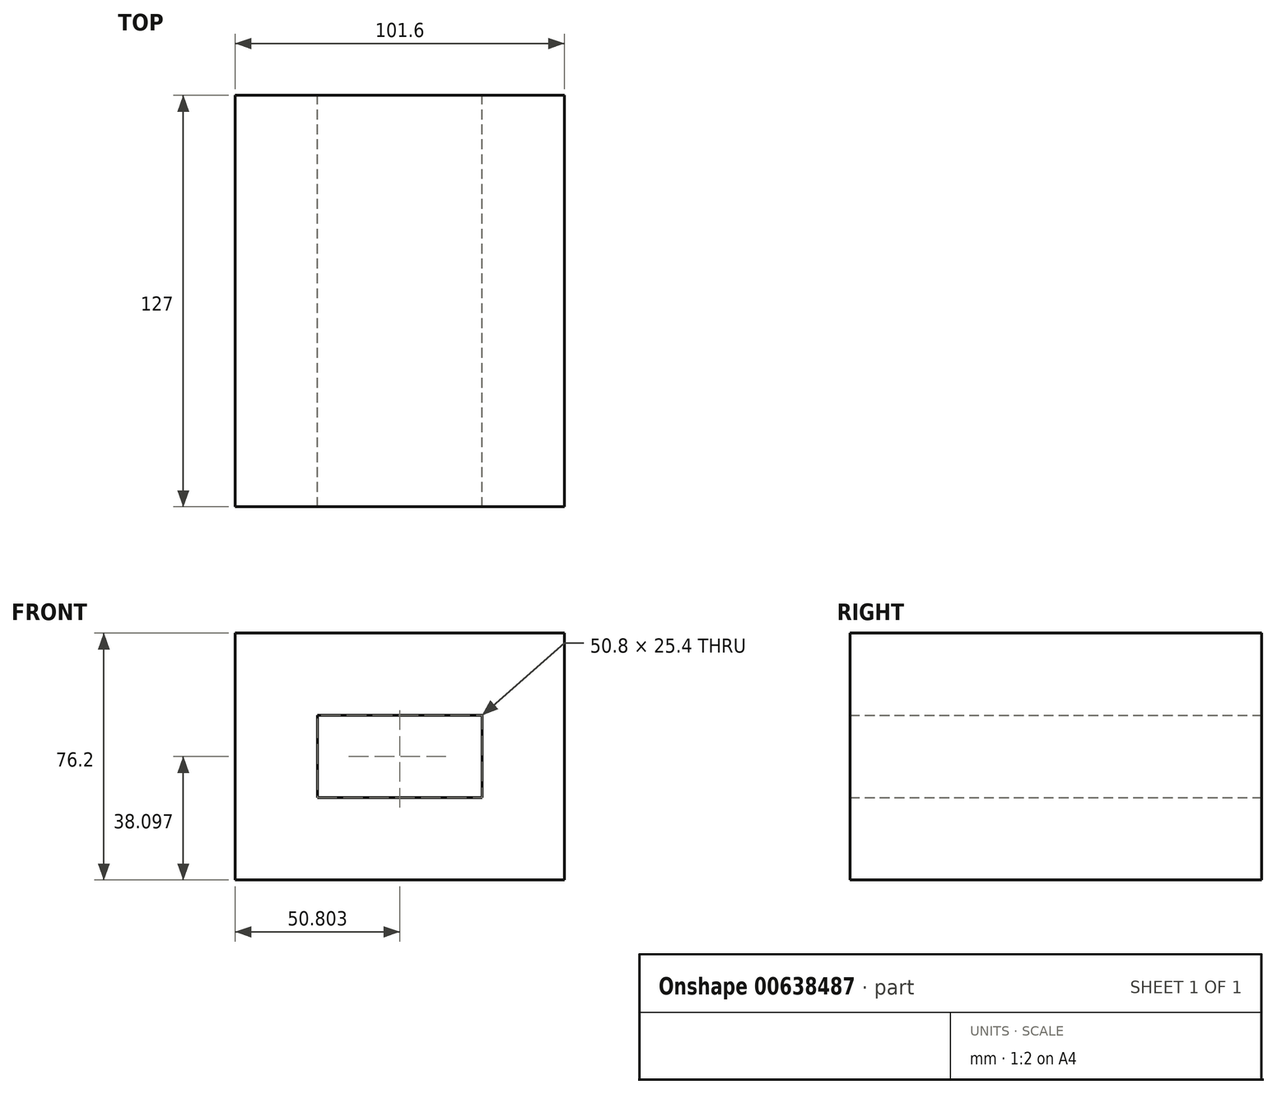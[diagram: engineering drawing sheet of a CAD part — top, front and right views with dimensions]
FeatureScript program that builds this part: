
annotation { "Feature Type Name" : "Feature", "Feature Type Description" : "" }
export const myFeature = defineFeature(function(context is Context, id is Id, definition is map)
    precondition{}
    {
        {
            var Q0;
            Q0=qCreatedBy(makeId("Front.planeOp"),FACE);
            var sketch = newSketch(context, id + "F0", { "sketchPlane" : qUnion([Q0])});
            skLineSegment(sketch, "E0.bottom", {"start": v(51.5, 37.5) * mm, "end": v(-50.1, 37.5) * mm});
            skLineSegment(sketch, "E0.top", {"start": v(51.5, -38.7) * mm, "end": v(-50.1, -38.7) * mm});
            skLineSegment(sketch, "E0.left", {"start": v(51.5, 37.5) * mm, "end": v(51.5, -38.7) * mm});
            skLineSegment(sketch, "E0.right", {"start": v(-50.1, 37.5) * mm, "end": v(-50.1, -38.7) * mm});
            skLineSegment(sketch, "E1.bottom", {"start": v(26.1, 12.1) * mm, "end": v(-24.7, 12.1) * mm});
            skLineSegment(sketch, "E1.top", {"start": v(26.1, -13.3) * mm, "end": v(-24.7, -13.3) * mm});
            skLineSegment(sketch, "E1.left", {"start": v(26.1, 12.1) * mm, "end": v(26.1, -13.3) * mm});
            skLineSegment(sketch, "E1.right", {"start": v(-24.7, 12.1) * mm, "end": v(-24.7, -13.3) * mm});
            skSolve(sketch);
        }
        {
            var Q0;
            Q0=makeQuery(id+"F0.imprint","IMPRINT",FACE,{"disambiguationData":[TD([[makeQuery(id+"F0.imprint","IMPRINT",EDGE,{"derivedFrom":sQuery(id+"F0.wireOp",EDGE,"E0.bottom")}),1.0]])]});
            extrude(context, id + "F1", {"entities" : qUnion([Q0]), "depth" : 127 * mm, "offsetDistance" : 25.4 * mm});
        }
    });
